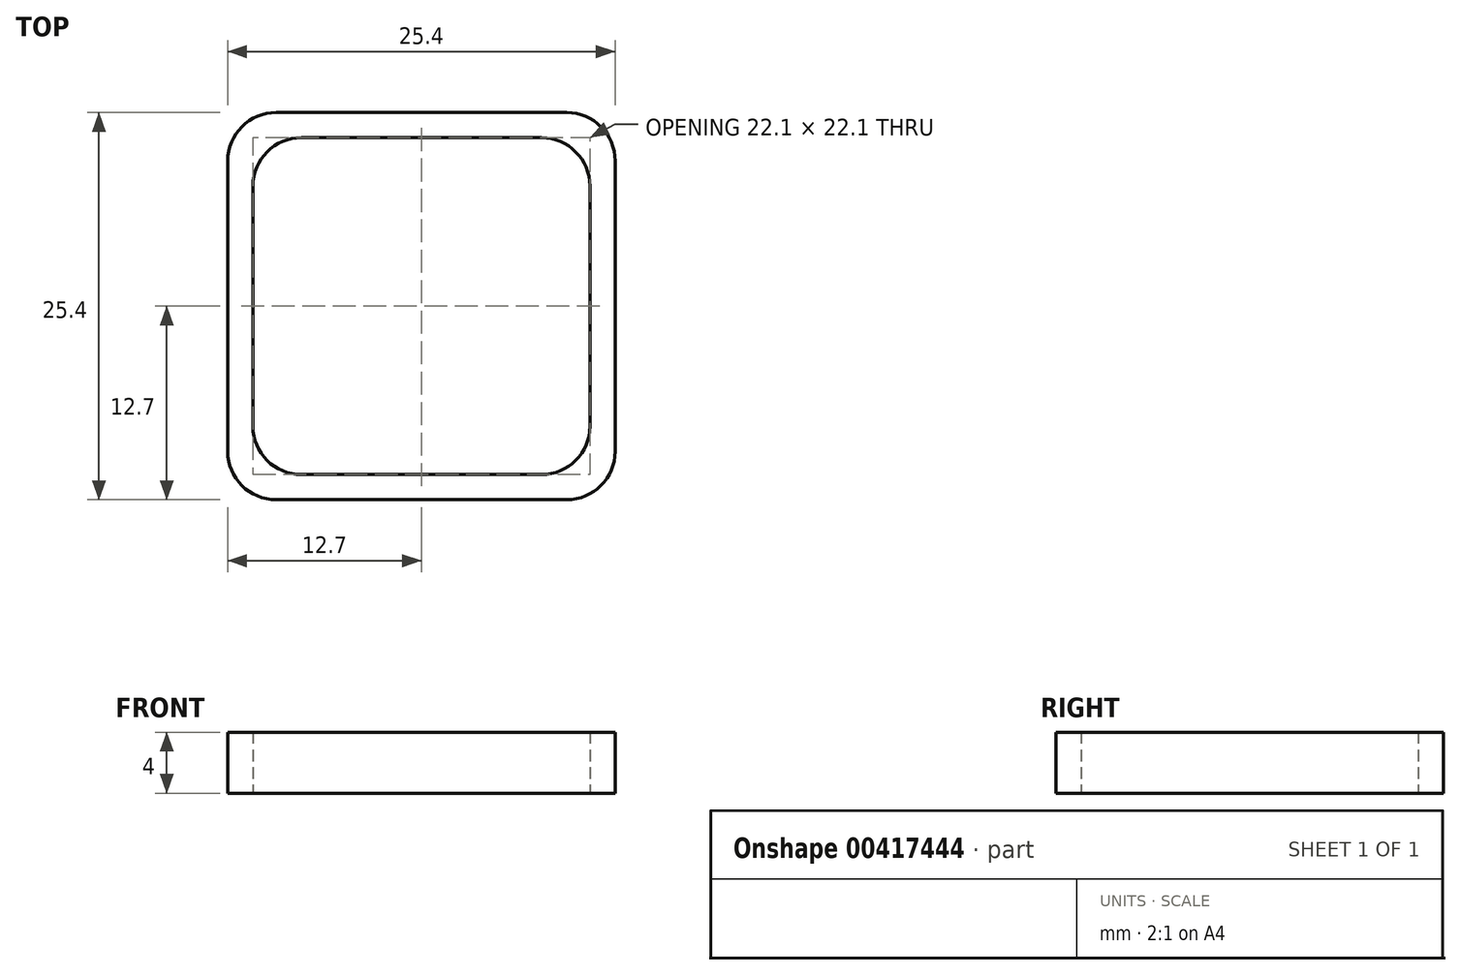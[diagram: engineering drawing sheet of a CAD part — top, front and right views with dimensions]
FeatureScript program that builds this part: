
annotation { "Feature Type Name" : "Feature", "Feature Type Description" : "" }
export const myFeature = defineFeature(function(context is Context, id is Id, definition is map)
    precondition{}
    {
        {
            assignVariable(context, id + "F0", {"name" : "BeamHeight", "anyValue" : 4});
        }
        {
            var Q0;
            Q0=qCreatedBy(makeId("Top.planeOp"),FACE);
            var sketch = newSketch(context, id + "F1", { "sketchPlane" : qUnion([Q0])});
            skPoint(sketch, "E0.middle", {"position": v(0, 0) * mm});
            skPoint(sketch, "E1.visualSharp", {"position": v(-12.7, 12.7) * mm});
            skPoint(sketch, "E2.visualSharp", {"position": v(12.7, 12.7) * mm});
            skPoint(sketch, "E3.visualSharp", {"position": v(12.7, -12.7) * mm});
            skPoint(sketch, "E4.visualSharp", {"position": v(-12.7, -12.7) * mm});
            skLineSegment(sketch, "E5.bottom", {"start": v(-7.87, 11.05) * mm, "end": v(7.87, 11.05) * mm});
            skLineSegment(sketch, "E5.top", {"start": v(-7.87, -11.05) * mm, "end": v(7.87, -11.05) * mm});
            skLineSegment(sketch, "E5.left", {"start": v(-11.05, 7.87) * mm, "end": v(-11.05, -7.87) * mm});
            skLineSegment(sketch, "E5.right", {"start": v(11.05, 7.87) * mm, "end": v(11.05, -7.87) * mm});
            skPoint(sketch, "E6.visualSharp", {"position": v(-11.05, 11.05) * mm});
            skArc(sketch, "E6.filletArc", {"start": v(-7.87, 11.05) * mm, "mid": v(-10.12, 10.12) * mm, "end": v(-11.05, 7.87) * mm});
            skPoint(sketch, "E7.visualSharp", {"position": v(11.05, 11.05) * mm});
            skArc(sketch, "E7.filletArc", {"start": v(11.05, 7.87) * mm, "mid": v(10.12, 10.12) * mm, "end": v(7.87, 11.05) * mm});
            skPoint(sketch, "E8.visualSharp", {"position": v(11.05, -11.05) * mm});
            skArc(sketch, "E8.filletArc", {"start": v(7.87, -11.05) * mm, "mid": v(10.12, -10.12) * mm, "end": v(11.05, -7.87) * mm});
            skPoint(sketch, "E9.visualSharp", {"position": v(-11.05, -11.05) * mm});
            skArc(sketch, "E9.filletArc", {"start": v(-11.05, -7.87) * mm, "mid": v(-10.12, -10.12) * mm, "end": v(-7.87, -11.05) * mm});
            skLineSegment(sketch, "E10.bottom", {"start": v(-12.7, 12.7) * mm, "end": v(12.7, 12.7) * mm});
            skLineSegment(sketch, "E10.top", {"start": v(-12.7, -12.7) * mm, "end": v(12.7, -12.7) * mm});
            skLineSegment(sketch, "E10.left", {"start": v(-12.7, 12.7) * mm, "end": v(-12.7, -12.7) * mm});
            skLineSegment(sketch, "E10.right", {"start": v(12.7, 12.7) * mm, "end": v(12.7, -12.7) * mm});
            skSolve(sketch);
        }
        {
            var Q0;
            Q0=makeQuery(id+"F1.imprint","IMPRINT",FACE,{"disambiguationData":[TD([[makeQuery(id+"F1.imprint","IMPRINT",EDGE,{"derivedFrom":sQuery(id+"F1.wireOp",EDGE,"E5.bottom")}),1.0]])]});
            extrude(context, id + "F2", {"entities" : qUnion([Q0]), "depth" : (getVariable(context, 'BeamHeight')) * mm});
        }
        {
            var Q0;
            Q0=makeQuery(id+"F2.opExtrude","SWEPT_FACE",FACE,{"disambiguationData":[OSD([sQuery(id+"F1.wireOp",EDGE,"E10.top")])]});
            var sketch = newSketch(context, id + "F3", { "sketchPlane" : qUnion([Q0])});
            skLineSegment(sketch, "E11", {"start": v(-12.7, 0) * mm, "end": v(12.7, 10.52) * mm});
            skLineSegment(sketch, "E12", {"start": v(12.7, 10.52) * mm, "end": v(12.7, 0) * mm});
            skLineSegment(sketch, "E13", {"start": v(12.7, 0) * mm, "end": v(-12.7, 0) * mm});
            skLineSegment(sketch, "E14", {"start": v(-12.7, 101.6) * mm, "end": v(12.7, 91.08) * mm});
            skLineSegment(sketch, "E15", {"start": v(12.7, 91.08) * mm, "end": v(12.7, 101.6) * mm});
            skLineSegment(sketch, "E16", {"start": v(12.7, 101.6) * mm, "end": v(-12.7, 101.6) * mm});
            skSolve(sketch);
        }
        {
            var Q0;
            Q0=makeQuery(id+"F3.imprint","IMPRINT",FACE,{"disambiguationData":[TD([[makeQuery(id+"F3.imprint","IMPRINT",EDGE,{"derivedFrom":sQuery(id+"F3.wireOp",EDGE,"E11")}),-1.0]])]});
            var Q1;
            Q1=makeQuery(id+"F3.imprint","IMPRINT",FACE,{"disambiguationData":[TD([[makeQuery(id+"F3.imprint","IMPRINT",EDGE,{"derivedFrom":sQuery(id+"F3.wireOp",EDGE,"E14")}),1.0]])]});
            extrude(context, id + "F4", {"entities" : qUnion([Q0, Q1]), "operationType" : NewBodyOperationType.REMOVE, "oppositeDirection" : true, "depth" : 25.4 * mm});
        }
        {
            var Q0;
            Q0=makeQuery(id+"F2.opExtrude","SWEPT_EDGE",EDGE,{"disambiguationData":[OSD([sQuery(id+"F1.wireOp",EDGE,"E10.bottom"),sQuery(id+"F1.wireOp",EDGE,"E10.left")])]});
            var Q1;
            Q1=makeQuery(id+"F2.opExtrude","SWEPT_EDGE",EDGE,{"disambiguationData":[OSD([sQuery(id+"F1.wireOp",EDGE,"E10.bottom"),sQuery(id+"F1.wireOp",EDGE,"E10.right")])]});
            var Q2;
            Q2=makeQuery(id+"F2.opExtrude","SWEPT_EDGE",EDGE,{"disambiguationData":[OSD([sQuery(id+"F1.wireOp",EDGE,"E10.top"),sQuery(id+"F1.wireOp",EDGE,"E10.left")])]});
            var Q3;
            Q3=makeQuery(id+"F2.opExtrude","SWEPT_EDGE",EDGE,{"disambiguationData":[OSD([sQuery(id+"F1.wireOp",EDGE,"E10.top"),sQuery(id+"F1.wireOp",EDGE,"E10.right")])]});
            fillet(context, id + "F5", {"entities" : qUnion([Q0, Q1, Q2, Q3]), "radius" : 3.17 * mm, "tangentPropagation" : true, "allowEdgeOverflow" : false});
        }
        {
            var Q0;
            Q0=makeQuery(id+"F2.opExtrude","SWEPT_FACE",FACE,{"disambiguationData":[OSD([sQuery(id+"F1.wireOp",EDGE,"E10.top")])]});
            var sketch = newSketch(context, id + "F6", { "sketchPlane" : qUnion([Q0])});
            skCircle(sketch, "E17", {"center": v(0, 50.8) * mm, "radius": 6.74 * mm});
            skLineSegment(sketch, "E18", {"start": v(-9.53, 50.8) * mm, "end": v(9.53, 50.8) * mm, "construction": true});
            skSolve(sketch);
        }
        {
            var Q0;
            Q0=makeQuery(id+"F6.imprint","IMPRINT",FACE,{"disambiguationData":[TD([[makeQuery(id+"F6.imprint","IMPRINT",EDGE,{"derivedFrom":sQuery(id+"F6.wireOp",EDGE,"E17")}),1.0]])]});
            extrude(context, id + "F7", {"entities" : qUnion([Q0]), "operationType" : NewBodyOperationType.REMOVE, "endBound" : BoundingType.THROUGH_ALL, "oppositeDirection" : true, "depth" : 25.4 * mm, "offsetDistance" : 25.4 * mm});
        }
    });
